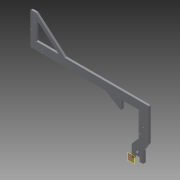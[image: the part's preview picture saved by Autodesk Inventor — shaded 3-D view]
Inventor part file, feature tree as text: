
AUTODESK INVENTOR PART (.ipt)
format: ipt  version: 2013 (Build 170138000, 138)  size: 206,848 bytes
history: native  units: in
note: dims shown in document units (in); Inventor stores cm internally (conversion verified against a paired STEP export)
features: extrude x4, sketch x3, plane x2, fillet x2
ambient origin geometry x8: Origin, YZ Plane, XZ Plane, XY Plane, X Axis, Y Axis, Z Axis, Center Point
feature tree (11):
  plane  "Work Plane4"
  plane  "Work Plane3"
  extrude  "Extrusion9"  Depth=1.25in
  extrude  "Extrusion10"  Depth=2.0in
  extrude  "Extrusion11"  Depth=0.75in
  fillet  "Fillet8"  Radius=1.5in
  fillet  "Fillet9"  [1 undecoded]
  extrude  "Extrusion12"  Depth=2.15in
  sketch  "Sketch8"  dims[d0=0.25in d1=0.5in d2=0.75in d3=0.25in d4=0.5in d5=0.3765in d6=0.5in d8=14.875in d17=4.0833in d19=0.375in d25=1.25in]
  sketch  "Sketch9"  dims[d26=0.125in d27=2.0in]
  sketch  "Sketch10"  dims[d28=1.0in d29=1.0in d30=0.75in d63=1.5in d68=0.0in d69=2.15in d71=0.875in d72=0.0in d73=6.625in d74=3.125in d75=3.0833in d76=9.475in d87=0.25in d88=1.5in d89=1.0in d91=1.0in d93=0.2797in d94=0.5in d95=0.75in d96=1.0in d97=0.2797in d98=10.5406in d99=0.25in d100=0.0in d101=0.15in d102=0.15in d103=0.573in d104=1.113in d105=0.175in d106=2.019in d107=0.25in d108=0.0in d109=0.125in d110=0.125in d111=1.5in d112=1.5in d113=0.25in d114=0.25in d115=0.125in d116=0.125in d117=1.5in d118=1.5in d119=0.1875in d121=0.25in d122=0.0in d123=0.125in d124=0.3125in d125=0.125in d126=1.5in d127=0.15in d128=0.15in d129=0.398in d130=0.906in d131=0.125in d132=0.125in d133=0.25in d134=0.0in]
note: 1 required parameter value undecoded (feature->parameter linkage not recoverable at this tier; creation-order binding heuristic only, values carry confidence <= 0.55)
